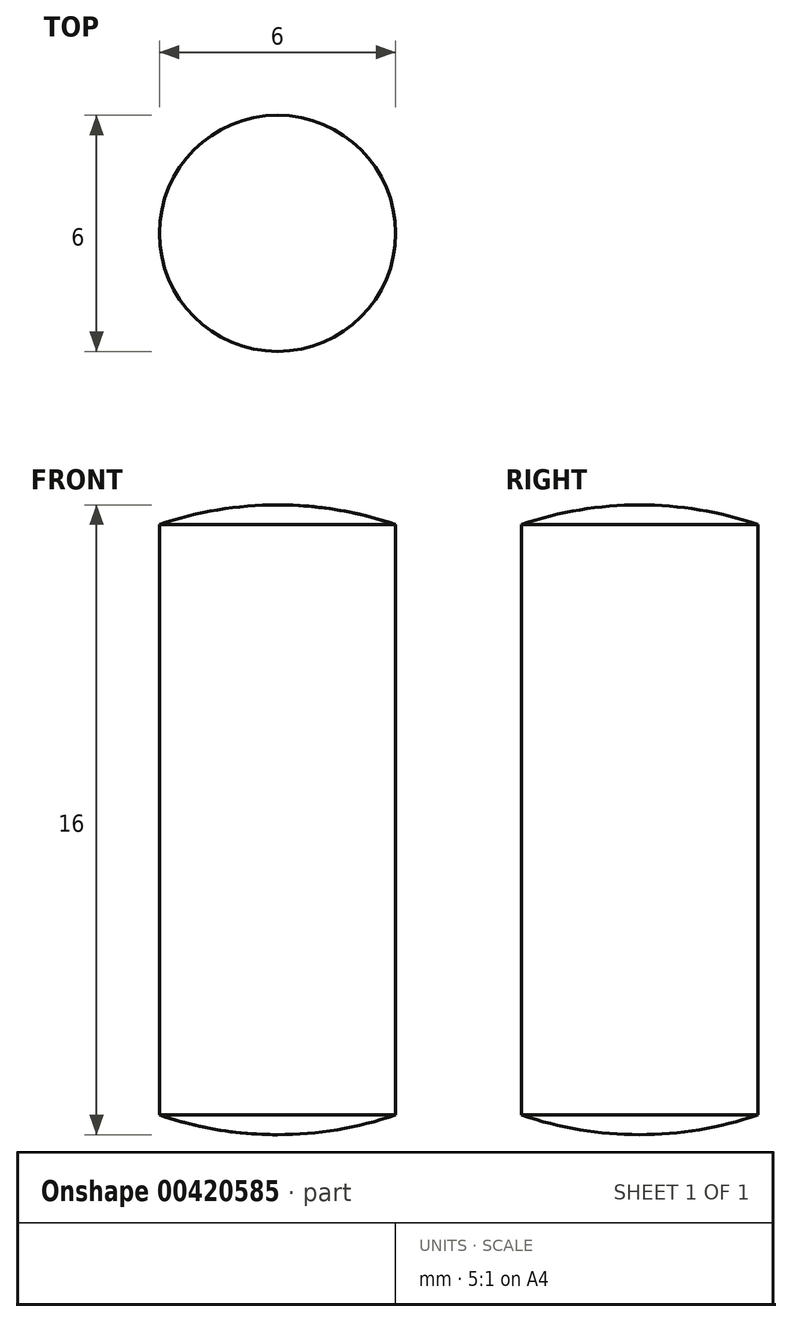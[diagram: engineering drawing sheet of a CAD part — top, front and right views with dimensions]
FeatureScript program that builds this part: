
annotation { "Feature Type Name" : "Feature", "Feature Type Description" : "" }
export const myFeature = defineFeature(function(context is Context, id is Id, definition is map)
    precondition{}
    {
        {
            var Q0;
            Q0=qCreatedBy(makeId("Front.planeOp"),FACE);
            var sketch = newSketch(context, id + "F0", { "sketchPlane" : qUnion([Q0])});
            skLineSegment(sketch, "E0", {"start": v(0, 0) * mm, "end": v(0, 18.01) * mm, "construction": true});
            skLineSegment(sketch, "E1", {"start": v(-3, 0.5) * mm, "end": v(-3, 15.5) * mm});
            skArc(sketch, "E2", {"start": v(-3, 0.5) * mm, "mid": v(-1.52, 0.13) * mm, "end": v(0, 0) * mm});
            skLineSegment(sketch, "E3", {"start": v(0, 0) * mm, "end": v(-7.45, 0) * mm, "construction": true});
            skLineSegment(sketch, "E4", {"start": v(0, 16) * mm, "end": v(-8.34, 16) * mm, "construction": true});
            skLineSegment(sketch, "E5", {"start": v(0, 16) * mm, "end": v(0, 0) * mm});
            skArc(sketch, "E6", {"start": v(0, 16) * mm, "mid": v(-1.52, 15.87) * mm, "end": v(-3, 15.5) * mm});
            skSolve(sketch);
        }
        {
            var Q0;
            Q0 = qSketchRegion(id + "F0", true);
            var Q1;
            Q1=sQuery(id+"F0.wireOp",EDGE,"E0");
            revolve(context, id + "F1", {"entities" : qUnion([Q0]), "axis" : qUnion([Q1]), "revolveType" : RevolveType.FULL});
        }
    });
